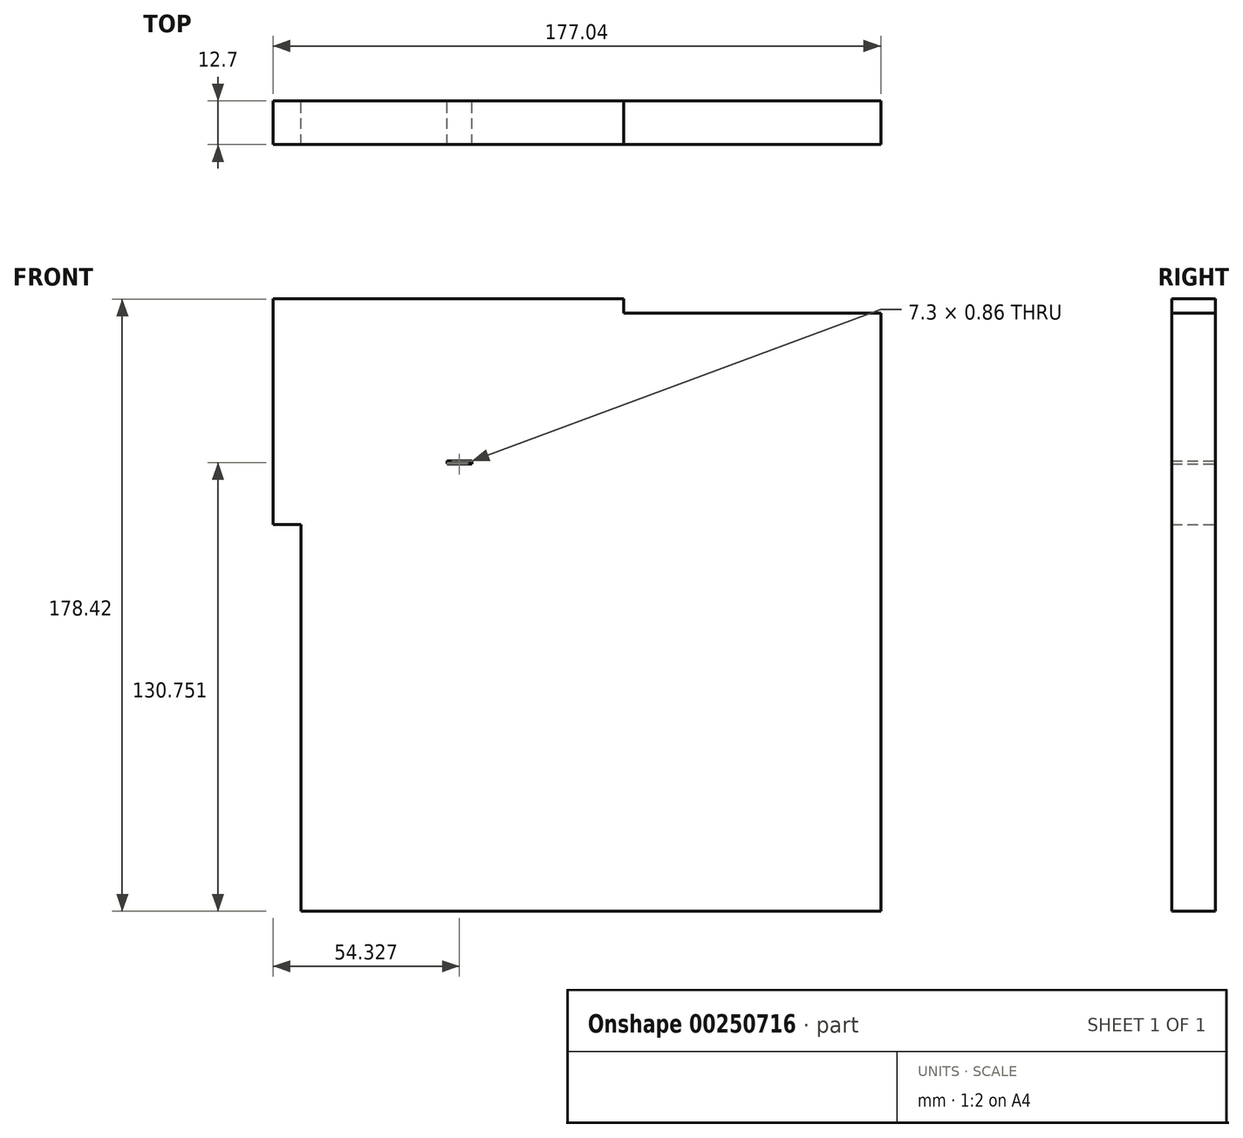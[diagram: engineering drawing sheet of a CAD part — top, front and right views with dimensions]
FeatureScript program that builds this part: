
annotation { "Feature Type Name" : "Feature", "Feature Type Description" : "" }
export const myFeature = defineFeature(function(context is Context, id is Id, definition is map)
    precondition{}
    {
        {
            var Q0;
            Q0=qCreatedBy(makeId("Front.planeOp"),FACE);
            var sketch = newSketch(context, id + "F0", { "sketchPlane" : qUnion([Q0])});
            skLineSegment(sketch, "E0.bottom", {"start": v(38.1, -35.81) * mm, "end": v(-130.76, -35.81) * mm});
            skLineSegment(sketch, "E0.top", {"start": v(38.1, 138.53) * mm, "end": v(-130.76, 138.53) * mm});
            skLineSegment(sketch, "E0.left", {"start": v(38.1, -35.81) * mm, "end": v(38.1, 138.53) * mm});
            skLineSegment(sketch, "E0.right", {"start": v(-130.76, -35.81) * mm, "end": v(-130.76, 138.53) * mm});
            skPoint(sketch, "E0.middle", {"position": v(-46.33, 51.36) * mm});
            skLineSegment(sketch, "E1.bottom", {"start": v(-88.26, 94.51) * mm, "end": v(-80.96, 94.51) * mm});
            skLineSegment(sketch, "E1.top", {"start": v(-88.26, 95.37) * mm, "end": v(-80.96, 95.37) * mm});
            skLineSegment(sketch, "E1.left", {"start": v(-88.26, 94.51) * mm, "end": v(-88.26, 95.37) * mm});
            skLineSegment(sketch, "E1.right", {"start": v(-80.96, 94.51) * mm, "end": v(-80.96, 95.37) * mm});
            skLineSegment(sketch, "E2.bottom", {"start": v(-138.94, 142.61) * mm, "end": v(-36.73, 142.61) * mm});
            skLineSegment(sketch, "E2.top", {"start": v(-138.94, 76.9) * mm, "end": v(-36.73, 76.9) * mm});
            skLineSegment(sketch, "E2.left", {"start": v(-138.94, 142.61) * mm, "end": v(-138.94, 76.9) * mm});
            skLineSegment(sketch, "E2.right", {"start": v(-36.73, 142.61) * mm, "end": v(-36.73, 76.9) * mm});
            skSolve(sketch);
        }
        {
            var Q0;
            Q0 = qSketchRegion(id + "F0", true);
            extrude(context, id + "F1", {"entities" : qUnion([Q0]), "depth" : 25.4 * mm});
        }
        {
            var Q0;
            Q0=makeQuery(id+"F1.opExtrude","CAP_FACE",FACE,{"disambiguationData":[OSD([sQuery(id+"F0.wireOp",EDGE,"E0.bottom"),sQuery(id+"F0.wireOp",EDGE,"E0.top"),sQuery(id+"F0.wireOp",EDGE,"E0.left"),sQuery(id+"F0.wireOp",EDGE,"E0.right")])],"isStart":false});
            extrude(context, id + "F2", {"entities" : qUnion([Q0]), "operationType" : NewBodyOperationType.REMOVE, "endBound" : BoundingType.SYMMETRIC, "oppositeDirection" : true, "depth" : 25.4 * mm});
        }
    });
